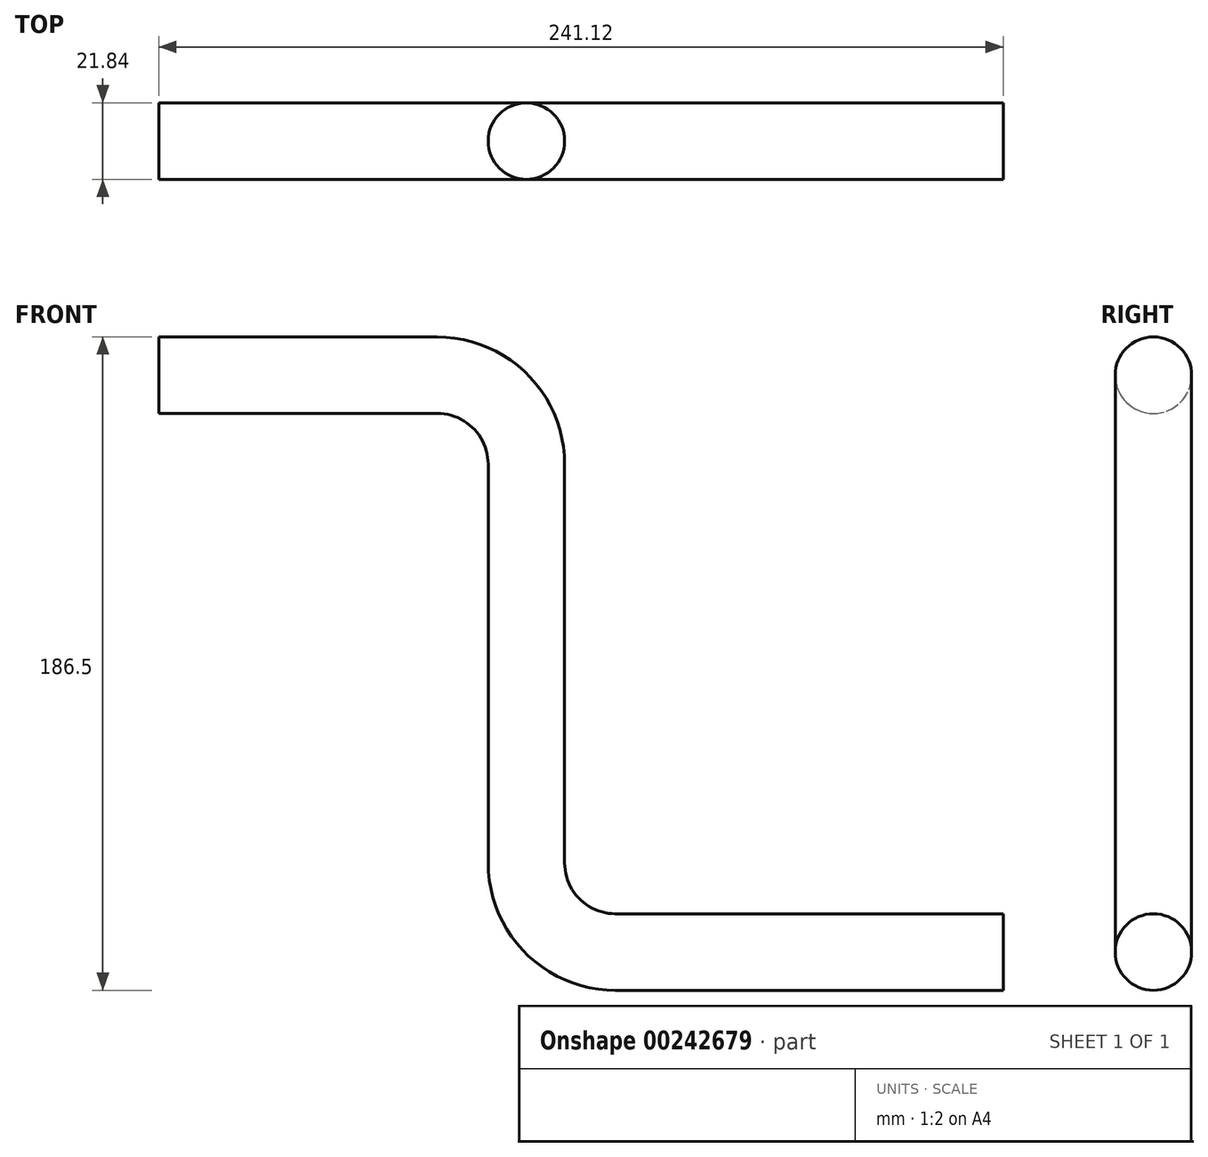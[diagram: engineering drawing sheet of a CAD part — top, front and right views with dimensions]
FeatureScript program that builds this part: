
annotation { "Feature Type Name" : "Feature", "Feature Type Description" : "" }
export const myFeature = defineFeature(function(context is Context, id is Id, definition is map)
    precondition{}
    {
        {
            var Q0;
            Q0=qCreatedBy(makeId("Right.planeOp"),FACE);
            var sketch = newSketch(context, id + "F0", { "sketchPlane" : qUnion([Q0])});
            skCircle(sketch, "E0", {"center": v(0, 0) * mm, "radius": 10.92 * mm});
            skSolve(sketch);
        }
        {
            var Q0;
            Q0=qCreatedBy(makeId("Front.planeOp"),FACE);
            var sketch = newSketch(context, id + "F1", { "sketchPlane" : qUnion([Q0])});
            skLineSegment(sketch, "E1", {"start": v(0, 0) * mm, "end": v(-110.75, 0) * mm});
            skLineSegment(sketch, "E2", {"start": v(-136.15, 25.4) * mm, "end": v(-136.15, 139.27) * mm});
            skLineSegment(sketch, "E3", {"start": v(-161.55, 164.67) * mm, "end": v(-241.12, 164.67) * mm});
            skPoint(sketch, "E4.visualSharp", {"position": v(-136.15, 164.67) * mm});
            skArc(sketch, "E4.filletArc", {"start": v(-136.15, 139.27) * mm, "mid": v(-143.6, 157.23) * mm, "end": v(-161.55, 164.67) * mm});
            skPoint(sketch, "E5.visualSharp", {"position": v(-136.15, 0) * mm});
            skArc(sketch, "E5.filletArc", {"start": v(-136.15, 25.4) * mm, "mid": v(-128.72, 7.44) * mm, "end": v(-110.75, 0) * mm});
            skSolve(sketch);
        }
        {
            var Q0;
            Q0=makeQuery(id+"F0.imprint","IMPRINT",FACE,{"disambiguationData":[TD([[makeQuery(id+"F0.imprint","IMPRINT",EDGE,{"derivedFrom":sQuery(id+"F0.wireOp",EDGE,"E0")}),1.0]])]});
            var Q1;
            Q1=sQuery(id+"F1.wireOp",EDGE,"E1");
            var Q2;
            Q2=sQuery(id+"F1.wireOp",EDGE,"E5.filletArc");
            var Q3;
            Q3=sQuery(id+"F1.wireOp",EDGE,"E2");
            var Q4;
            Q4=sQuery(id+"F1.wireOp",EDGE,"E4.filletArc");
            var Q5;
            Q5=sQuery(id+"F1.wireOp",EDGE,"E3");
            sweep(context, id + "F2", {"profiles" : qUnion([Q0]), "path" : qUnion([Q1, Q2, Q3, Q4, Q5])});
        }
    });
